# Revit family: signalizator magnitokontaktnyy SMK-1
name_source: partatom
category: Датчики
units: mm (PartAtom-declared; Revit-internal decimal feet)

## family parameters
Всегда вертикально = Да
Заголовок OmniClass = Communication and Data Processing Equipment
На основе рабочей плоскости = Нет
Номер OmniClass = 23.85.50.17
Общий = Нет
При загрузке вырезать с полостями = Нет
Размер круглого соединителя = Использовать диаметр
Сохранять ориентацию аннотаций = Нет
Тип детали = Нормальный
Точка принадлежности помещению = Нет

## types (1)
- Сигнализатор магнитоконтактный СМК-1
    ADSK_Единица измерения = шт.
    ADSK_Завод-изготовитель = ООО НПП «МАГНИТО-КОНТАКТ»
    ADSK_Масса = 0.12
    ADSK_Материал = Пластик
    ADSK_Наименование = Сигнализатор магнитоконтактный СМК-1
    ADSK_Наименование краткое = СМК-1
    ADSK_Обозначение = АТФЕ.425119.169
    ADSK_Примечание = Сигнализатор сохраняет работоспособность при температуре окружающего воздуха от -50°С до +50°С и относительной влажности до 98% при температуре +35°С без конденсации влаги.Сигнализатор рассчитан на непрерывную круглосуточную работу
    ADSK_Размер_Высота = 11 мм
    ADSK_Размер_Диаметр = 3 мм
    ADSK_Размер_Длина = 57 мм
    ADSK_Размер_Длина вывода = 100 мм
    ADSK_Размер_Ширина = 11 мм
    URL = https://m-kontakt.ru
    Выходное сопротивление = не более 0.5 Ом при токе пропускания (100±10) мА
    Изготовитель = ООО НПП «МАГНИТО-КОНТАКТ»
    Кабель = Да
    Описание = Сигнализатор магнитоконтактный СМК-1 предназначен для блокировки дверных и оконных проёмов, организации устройств типа «ловушка», а также блокировки других конструктивных элементов зданий и сооружений на открывание или смещение с выдачей сигнала «тревога» путём размыкания контактов геркона на приёмно-контрольный прибор, концентратор или пункт централизованного наблюдения.
    Отметка по умолчанию = 0 мм
    Срок службы = не менее 8 лет
    Степень защиты оболочки = IP44
    Число срабатываний = не менее 106 при максимальной мощности 10 Вт
